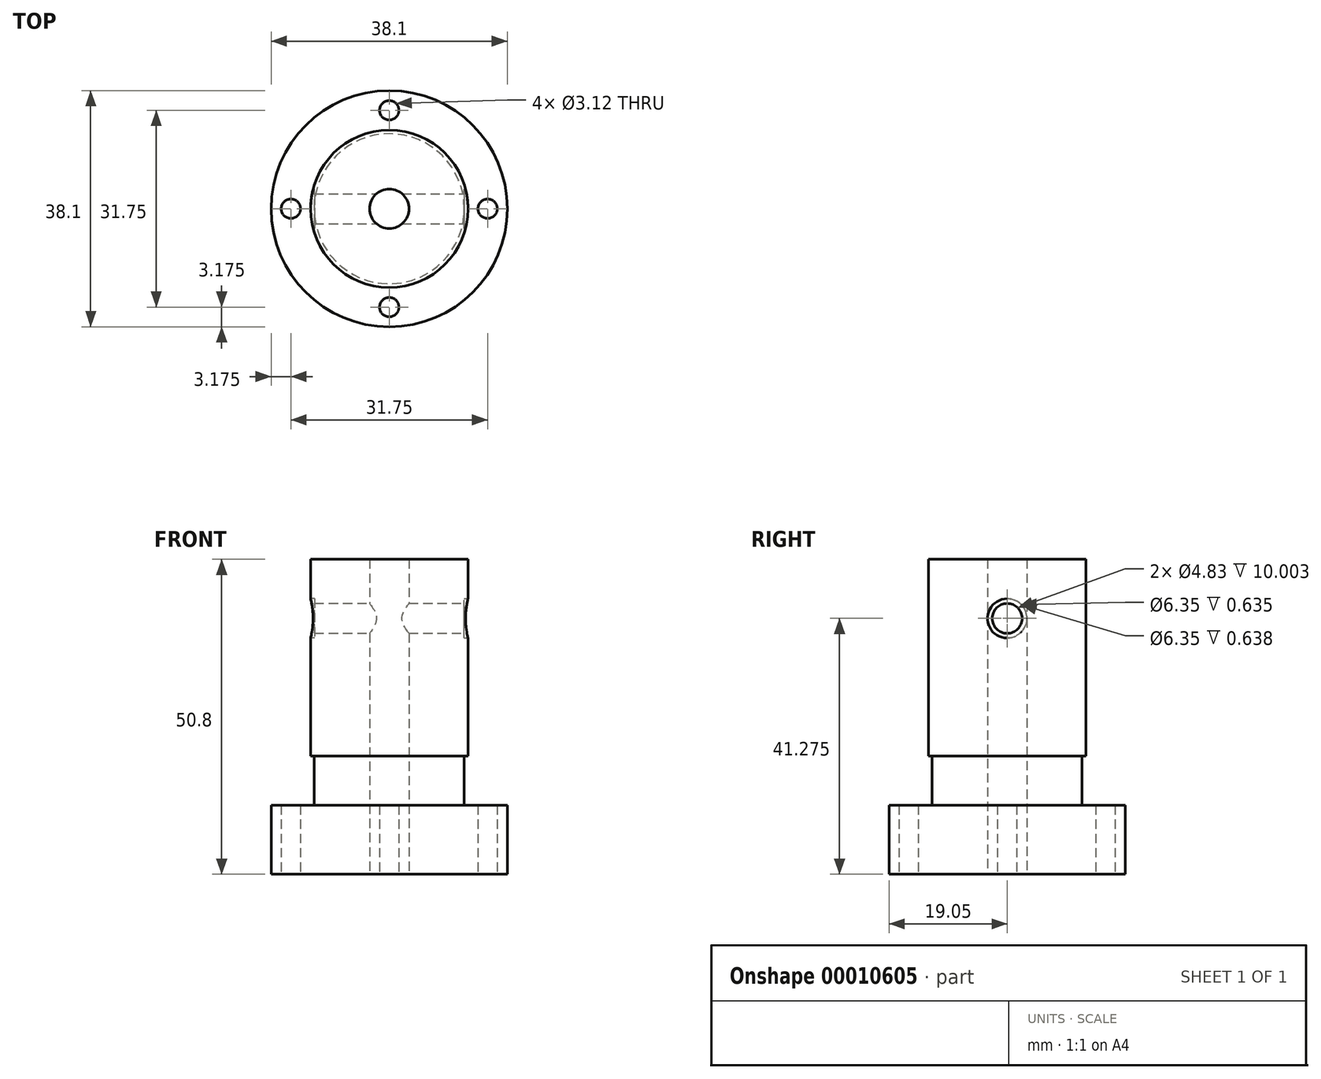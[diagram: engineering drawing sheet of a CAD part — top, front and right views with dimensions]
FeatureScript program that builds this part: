
annotation { "Feature Type Name" : "Feature", "Feature Type Description" : "" }
export const myFeature = defineFeature(function(context is Context, id is Id, definition is map)
    precondition{}
    {
        {
            var Q0;
            Q0=qCreatedBy(makeId("Top.planeOp"),FACE);
            var sketch = newSketch(context, id + "F0", { "sketchPlane" : qUnion([Q0])});
            skCircle(sketch, "E0", {"center": v(0, 0) * mm, "radius": 19.05 * mm});
            skCircle(sketch, "E1", {"center": v(0, 0) * mm, "radius": 15.88 * mm, "construction": true});
            skCircle(sketch, "E2", {"center": v(0, 0) * mm, "radius": 12.7 * mm});
            skCircle(sketch, "E3", {"center": v(0, 0) * mm, "radius": 12.1 * mm});
            skCircle(sketch, "E4", {"center": v(0, 0) * mm, "radius": 3.18 * mm});
            skLineSegment(sketch, "E5", {"start": v(0, 19.05) * mm, "end": v(0, -19.05) * mm, "construction": true});
            skLineSegment(sketch, "E6", {"start": v(-19.05, 0) * mm, "end": v(19.05, 0) * mm, "construction": true});
            skCircle(sketch, "E7", {"center": v(0, 15.88) * mm, "radius": 1.56 * mm});
            skCircle(sketch, "E8", {"center": v(-15.88, 0) * mm, "radius": 1.56 * mm});
            skCircle(sketch, "E9.0.MirrorC", {"center": v(15.88, 0) * mm, "radius": 1.56 * mm});
            skCircle(sketch, "E10.0.MirrorC", {"center": v(0, -15.88) * mm, "radius": 1.56 * mm});
            skSolve(sketch);
        }
        {
            var Q0;
            Q0=qSketchRegion(id+"F0",true);
            var Q1;
            Q1=makeQuery(id+"F0.imprint","IMPRINT",FACE,{"disambiguationData":[TD([[makeQuery(id+"F0.imprint","IMPRINT",EDGE,{"derivedFrom":sQuery(id+"F0.wireOp",EDGE,"E3")}),1.0]])]});
            var Q2;
            Q2=makeQuery(id+"F0.imprint","IMPRINT",FACE,{"disambiguationData":[TD([[makeQuery(id+"F0.imprint","IMPRINT",EDGE,{"derivedFrom":sQuery(id+"F0.wireOp",EDGE,"E2")}),1.0]])]});
            extrude(context, id + "F1", {"entities" : qUnion([Q0, Q1, Q2]), "depth" : 11.13 * mm});
        }
        {
            var Q0;
            Q0=makeQuery(id+"F1.opExtrude","CAP_FACE",FACE,{"disambiguationData":[OSD([sQuery(id+"F0.wireOp",EDGE,"E0"),sQuery(id+"F0.wireOp",EDGE,"E4"),sQuery(id+"F0.wireOp",EDGE,"E7"),sQuery(id+"F0.wireOp",EDGE,"E8"),sQuery(id+"F0.wireOp",EDGE,"E9.0.MirrorC"),sQuery(id+"F0.wireOp",EDGE,"E10.0.MirrorC")])],"isStart":false});
            var sketch = newSketch(context, id + "F2", { "sketchPlane" : qUnion([Q0])});
            skCircle(sketch, "E11.0", {"center": v(0, 0) * mm, "radius": 12.1 * mm});
            skCircle(sketch, "E12.0", {"center": v(0, 0) * mm, "radius": 3.18 * mm});
            skSolve(sketch);
        }
        {
            var Q0;
            Q0=qSketchRegion(id+"F2",true);
            extrude(context, id + "F3", {"entities" : qUnion([Q0]), "operationType" : NewBodyOperationType.ADD, "depth" : 7.95 * mm});
        }
        {
            var Q0;
            Q0=makeQuery(id+"F3.opExtrude","CAP_FACE",FACE,{"disambiguationData":[OSD([sQuery(id+"F2.wireOp",EDGE,"E11.0"),sQuery(id+"F2.wireOp",EDGE,"E12.0")])],"isStart":false});
            var sketch = newSketch(context, id + "F4", { "sketchPlane" : qUnion([Q0])});
            skCircle(sketch, "E13.0", {"center": v(0, 0) * mm, "radius": 12.7 * mm});
            skCircle(sketch, "E14.0", {"center": v(0, 0) * mm, "radius": 3.18 * mm});
            skSolve(sketch);
        }
        {
            var Q0;
            Q0=qSketchRegion(id+"F4",true);
            extrude(context, id + "F5", {"entities" : qUnion([Q0]), "operationType" : NewBodyOperationType.ADD, "depth" : 31.72 * mm});
        }
        {
            var Q0;
            Q0=qCreatedBy(makeId("Right.planeOp"),FACE);
            cPlane(context, id + "F6", {"entities" : qUnion([Q0]), "cplaneType" : CPlaneType.OFFSET, "offset" : 12.7 * mm, "width" : 152.4 * mm, "height" : 152.4 * mm});
        }
        {
            var Q0;
            Q0=qCreatedBy(id+"F6.planeOp",FACE);
            var sketch = newSketch(context, id + "F7", { "sketchPlane" : qUnion([Q0])});
            skLineSegment(sketch, "E15.0", {"start": v(-19.05, 0) * mm, "end": v(19.05, 0) * mm});
            skCircle(sketch, "E16", {"center": v(0, 41.28) * mm, "radius": 2.41 * mm});
            skCircle(sketch, "E17", {"center": v(0, 41.28) * mm, "radius": 3.18 * mm});
            skSolve(sketch);
        }
        {
            var Q0;
            Q0=makeQuery(id+"F7.imprint","IMPRINT",FACE,{"disambiguationData":[TD([[makeQuery(id+"F7.imprint","IMPRINT",EDGE,{"derivedFrom":sQuery(id+"F7.wireOp",EDGE,"E16")}),1.0]])]});
            extrude(context, id + "F8", {"entities" : qUnion([Q0]), "operationType" : NewBodyOperationType.REMOVE, "endBound" : BoundingType.THROUGH_ALL, "oppositeDirection" : true, "depth" : 25.4 * mm});
        }
        {
            var Q0;
            Q0=makeQuery(id+"F7.imprint","IMPRINT",FACE,{"disambiguationData":[TD([[makeQuery(id+"F7.imprint","IMPRINT",EDGE,{"derivedFrom":sQuery(id+"F7.wireOp",EDGE,"E16")}),-1.0]])]});
            var Q1;
            Q1=sQuery(id+"F7.wireOp",EDGE,"E17");
            extrude(context, id + "F9", {"entities" : qUnion([Q0]), "operationType" : NewBodyOperationType.REMOVE, "surfaceEntities" : qUnion([Q1]), "oppositeDirection" : true, "depth" : 0.64 * mm});
        }
        {
            var Q0;
            Q0=qCreatedBy(makeId("Right.planeOp"),FACE);
            cPlane(context, id + "F10", {"entities" : qUnion([Q0]), "cplaneType" : CPlaneType.OFFSET, "offset" : 12.7 * mm, "oppositeDirection" : true, "width" : 152.4 * mm, "height" : 152.4 * mm});
        }
        {
            var Q0;
            Q0=qCreatedBy(id+"F10.planeOp",FACE);
            var sketch = newSketch(context, id + "F11", { "sketchPlane" : qUnion([Q0])});
            skCircle(sketch, "E18.0", {"center": v(0, 41.28) * mm, "radius": 3.18 * mm});
            skCircle(sketch, "E19.0", {"center": v(0, 41.28) * mm, "radius": 2.41 * mm});
            skSolve(sketch);
        }
        {
            var Q0;
            Q0=qSketchRegion(id+"F11",true);
            extrude(context, id + "F12", {"entities" : qUnion([Q0]), "operationType" : NewBodyOperationType.REMOVE, "depth" : 0.64 * mm});
        }
    });
